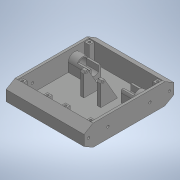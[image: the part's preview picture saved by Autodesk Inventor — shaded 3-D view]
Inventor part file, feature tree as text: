
AUTODESK INVENTOR PART (.ipt)
format: ipt  version: 2020 (Build 240168000, 168)  size: 377,344 bytes
history: native  units: in
note: dims shown in document units (in); Inventor stores cm internally (conversion verified against a paired STEP export)
features: projected_geometry x13, extrude x11, sketch x11, mirror x4, plane x1
ambient origin geometry x8: Origin, YZ Plane, XZ Plane, XY Plane, X Axis, Y Axis, Z Axis, Center Point
bodies: Solid1 (feature_tree)
feature tree (40):
  extrude  "Extrusion1"  Depth=5.9055in
  extrude  "Extrusion2"  TaperAngle=0.0deg  [1 undecoded]
  extrude  "Extrusion3"  Depth=1.2598in
  extrude  "Extrusion4"  Depth=0.315in
  extrude  "Extrusion5"  TaperAngle=0.0deg  [1 undecoded]
  extrude  "Extrusion6"  Depth=0.689in
  mirror  "Mirror1"
  extrude  "Extrusion7"  Depth=0.0787in
  mirror  "Mirror2"
  extrude  "Extrusion8"  Depth=0.5512in
  mirror  "Mirror3"
  plane  "Work Plane1"
  extrude  "Extrusion9"  Depth=0.7874in TaperAngle=0.0deg
  mirror  "Mirror4"
  extrude  "Extrusion10"  Depth=6.063in TaperAngle=0.0deg
  extrude  "Extrusion11"  Depth=0.1575in
  sketch  "Sketch1"  dims[d0=1.378in d1=5.9055in]
  sketch  "Sketch2"  dims[d2=5.1181in d3=0.0in]
  projected_geometry  "Projected Loop1"
  sketch  "Sketch3"  dims[d4=0.1575in d5=1.2598in]
  projected_geometry  "Projected Loop2"
  projected_geometry  "Projected Loop3"
  sketch  "Sketch4"  dims[d6=0.0in d8=0.315in]
  sketch  "Sketch5"  dims[d10=1.1898in d11=0.0in]
  projected_geometry  "Projected Loop4"
  sketch  "Sketch6"  dims[d12=0.6496in d13=0.689in]
  sketch  "Sketch7"  dims[d14=1.5748in d15=0.0787in]
  sketch  "Sketch9"  dims[d16=0.5512in d17=0.0in d18=0.6102in]
  sketch  "Sketch10"  dims[d19=0.4803in d20=0.7874in d21=0.0in]
  sketch  "Sketch12"  dims[d22=0.1654in d23=6.063in d24=0.0in]
  projected_geometry  "Projected Loop6"
  projected_geometry  "Projected Loop7"
  projected_geometry  "Projected Loop8"
  sketch  "Sketch13"  dims[d25=0.5967in d26=0.1575in d27=1.5748in d28=0.0in d29=0.0in d30=0.1575in d31=0.2756in d32=0.0in d33=0.4331in d34=0.122in d38=2.7559in d40=0.061in d41=0.0909in d42=0.2362in d43=0.0in d44=60.0deg d45=0.0787in d46=0.315in d48=1.1898in d49=0.0in d51=0.1575in d52=0.1575in d53=0.2756in d54=0.0in]
  projected_geometry  "Projected Loop9"
  projected_geometry  "Projected Loop10"
  projected_geometry  "Projected Loop11"
  projected_geometry  "Projected Loop12"
  projected_geometry  "Projected Loop13"
  projected_geometry  "Projected Loop14"
note: 2 required parameter values undecoded (feature->parameter linkage not recoverable at this tier; creation-order binding heuristic only, values carry confidence <= 0.55)
